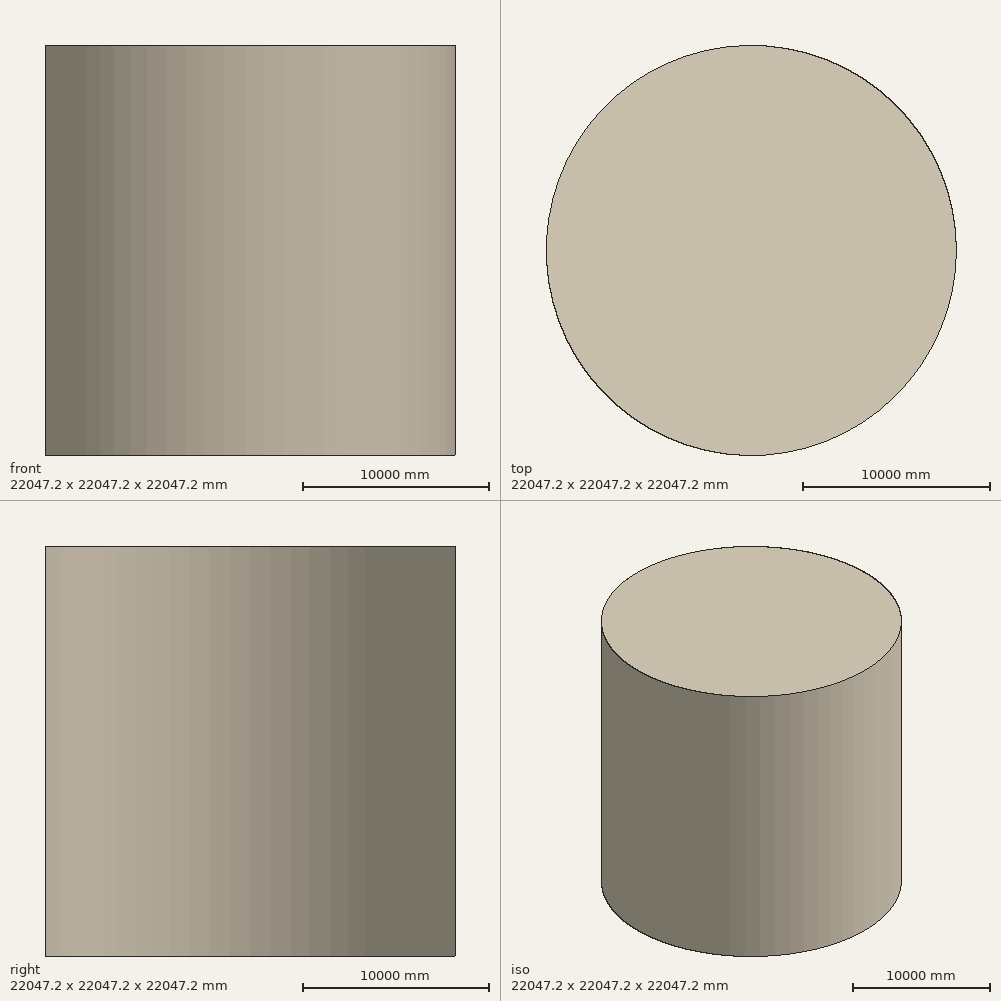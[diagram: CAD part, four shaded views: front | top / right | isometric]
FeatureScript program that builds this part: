
annotation { "Feature Type Name" : "Feature", "Feature Type Description" : "" }
export const myFeature = defineFeature(function(context is Context, id is Id, definition is map)
    precondition{}
    {
        {
            var Q0;
            Q0=qCreatedBy(makeId("Top.planeOp"),FACE);
            var sketch = newSketch(context, id + "F0", { "sketchPlane" : qUnion([Q0])});
            skCircle(sketch, "E0", {"center": v(0, 0) * mm, "radius": 11023.6 * mm});
            skSolve(sketch);
        }
        {
            var Q0;
            Q0=makeQuery(id+"F0.imprint","IMPRINT",FACE,{"disambiguationData":[TD([[makeQuery(id+"F0.imprint","IMPRINT",EDGE,{"derivedFrom":sQuery(id+"F0.wireOp",EDGE,"E0")}),1.0]])]});
            extrude(context, id + "F1", {"entities" : qUnion([Q0]), "depth" : 22047.2 * mm});
        }
    });
